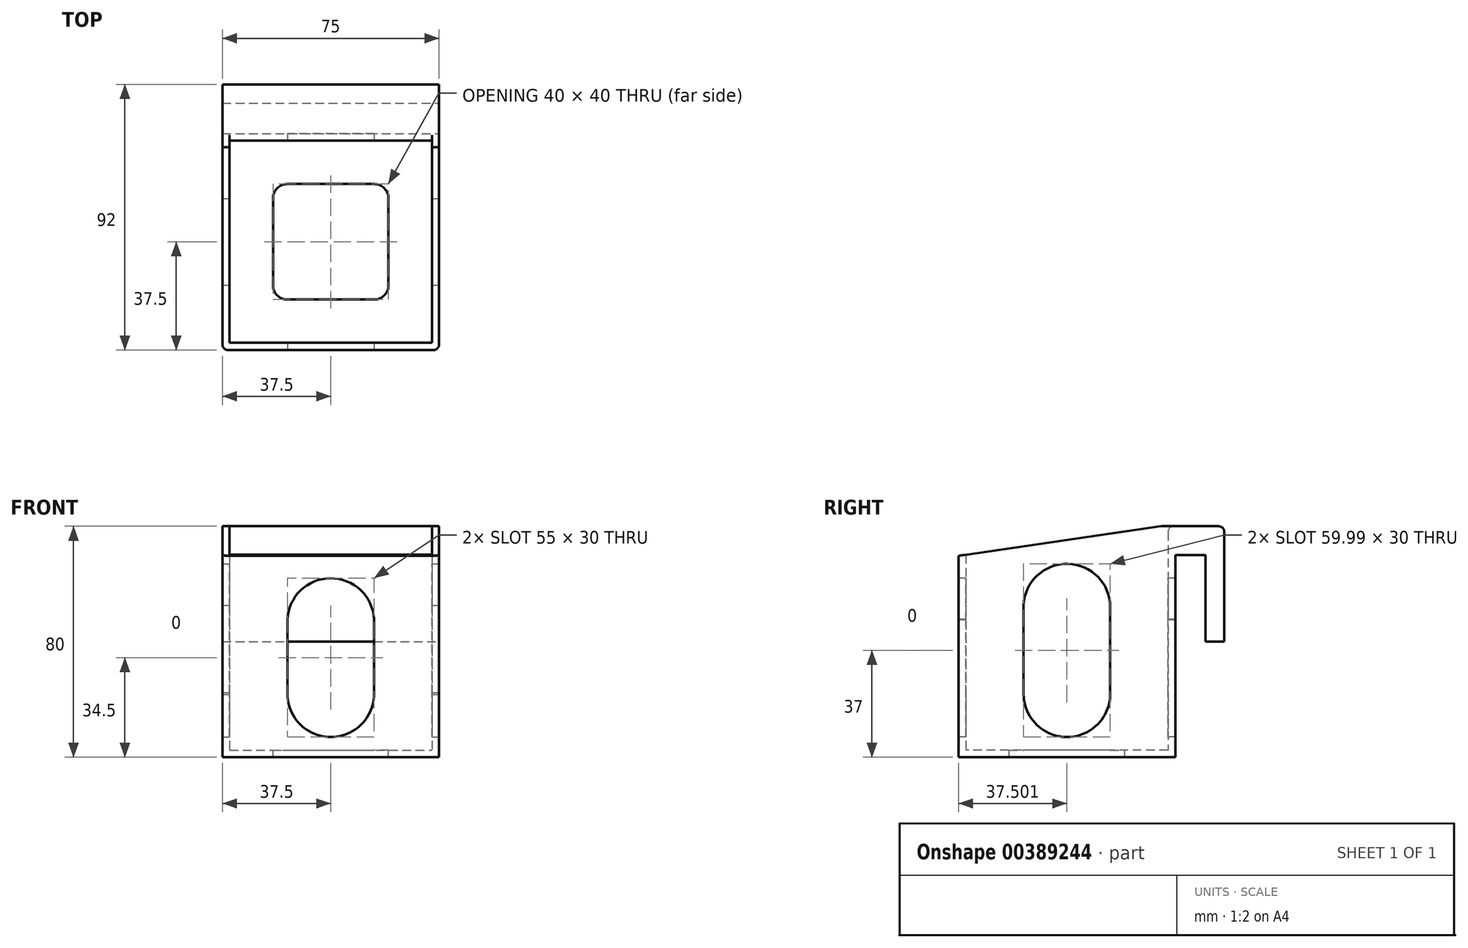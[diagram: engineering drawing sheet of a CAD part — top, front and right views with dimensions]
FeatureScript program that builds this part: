
annotation { "Feature Type Name" : "Feature", "Feature Type Description" : "" }
export const myFeature = defineFeature(function(context is Context, id is Id, definition is map)
    precondition{}
    {
        {
            var Q0;
            Q0=qCreatedBy(makeId("Top.planeOp"),FACE);
            var sketch = newSketch(context, id + "F0", { "sketchPlane" : qUnion([Q0])});
            skLineSegment(sketch, "E0.bottom", {"start": v(-35, 35) * mm, "end": v(35, 35) * mm});
            skLineSegment(sketch, "E0.top", {"start": v(-35, -35) * mm, "end": v(35, -35) * mm});
            skLineSegment(sketch, "E0.left", {"start": v(-35, 35) * mm, "end": v(-35, -35) * mm});
            skLineSegment(sketch, "E0.right", {"start": v(35, 35) * mm, "end": v(35, -35) * mm});
            skPoint(sketch, "E0.middle", {"position": v(0, 0) * mm});
            skLineSegment(sketch, "E1.0", {"start": v(-37.5, 37.5) * mm, "end": v(37.5, 37.5) * mm});
            skLineSegment(sketch, "E1.1", {"start": v(-37.5, 37.5) * mm, "end": v(-37.5, -37.5) * mm});
            skLineSegment(sketch, "E1.2", {"start": v(-37.5, -37.5) * mm, "end": v(37.5, -37.5) * mm});
            skLineSegment(sketch, "E1.3", {"start": v(37.5, 37.5) * mm, "end": v(37.5, -37.5) * mm});
            skSolve(sketch);
        }
        {
            var Q0;
            Q0 = qSketchRegion(id + "F0", true);
            var Q1;
            Q1=makeQuery(id+"F0.imprint","IMPRINT",FACE,{"disambiguationData":[TD([[makeQuery(id+"F0.imprint","IMPRINT",EDGE,{"derivedFrom":sQuery(id+"F0.wireOp",EDGE,"E0.bottom")}),-1.0]])]});
            extrude(context, id + "F1", {"entities" : qUnion([Q0, Q1]), "depth" : 80 * mm, "offsetDistance" : 25 * mm});
        }
        {
            var Q0;
            Q0=makeQuery(id+"F1.opExtrude","CAP_FACE",FACE,{"disambiguationData":[OSD([sQuery(id+"F0.wireOp",EDGE,"E1.0"),sQuery(id+"F0.wireOp",EDGE,"E1.1"),sQuery(id+"F0.wireOp",EDGE,"E1.2"),sQuery(id+"F0.wireOp",EDGE,"E1.3")])],"isStart":false});
            shell(context, id + "F2", {"entities" : qUnion([Q0]), "thickness" : 2.5 * mm});
        }
        {
            var Q0;
            Q0=makeQuery(id+"F1.opExtrude","SWEPT_FACE",FACE,{"disambiguationData":[OSD([sQuery(id+"F0.wireOp",EDGE,"E1.1")])]});
            var sketch = newSketch(context, id + "F3", { "sketchPlane" : qUnion([Q0])});
            skLineSegment(sketch, "E2", {"start": v(-32.69, 80) * mm, "end": v(37.5, 69.78) * mm});
            skLineSegment(sketch, "E3", {"start": v(37.5, 69.78) * mm, "end": v(37.5, 80) * mm});
            skLineSegment(sketch, "E4", {"start": v(37.5, 80) * mm, "end": v(-32.69, 80) * mm});
            skSolve(sketch);
        }
        {
            var Q0;
            Q0 = qSketchRegion(id + "F3", true);
            extrude(context, id + "F4", {"entities" : qUnion([Q0]), "operationType" : NewBodyOperationType.REMOVE, "endBound" : BoundingType.THROUGH_ALL, "oppositeDirection" : true, "depth" : 25 * mm, "offsetDistance" : 25 * mm});
        }
        {
            var Q0;
            Q0=makeQuery(id+"F1.opExtrude","SWEPT_FACE",FACE,{"disambiguationData":[OSD([sQuery(id+"F0.wireOp",EDGE,"E1.0")])]});
            var sketch = newSketch(context, id + "F5", { "sketchPlane" : qUnion([Q0])});
            skLineSegment(sketch, "E5.bottom", {"start": v(-37.5, 80) * mm, "end": v(37.5, 80) * mm});
            skLineSegment(sketch, "E5.top", {"start": v(-37.5, 40) * mm, "end": v(37.5, 40) * mm});
            skLineSegment(sketch, "E5.left", {"start": v(-37.5, 80) * mm, "end": v(-37.5, 40) * mm});
            skLineSegment(sketch, "E5.right", {"start": v(37.5, 80) * mm, "end": v(37.5, 40) * mm});
            skSolve(sketch);
        }
        {
            var Q0;
            Q0 = qSketchRegion(id + "F5", true);
            extrude(context, id + "F6", {"entities" : qUnion([Q0]), "operationType" : NewBodyOperationType.ADD, "depth" : 17 * mm, "offsetDistance" : 25 * mm});
        }
        {
            var Q0;
            Q0=makeQuery(id+"F6.opExtrude","SWEPT_FACE",FACE,{"disambiguationData":[OSD([sQuery(id+"F5.wireOp",EDGE,"E5.top")])]});
            var sketch = newSketch(context, id + "F7", { "sketchPlane" : qUnion([Q0])});
            skLineSegment(sketch, "E6.bottom", {"start": v(-37.5, -37.5) * mm, "end": v(37.5, -37.5) * mm});
            skLineSegment(sketch, "E6.top", {"start": v(-37.5, -48) * mm, "end": v(37.5, -48) * mm});
            skLineSegment(sketch, "E6.left", {"start": v(-37.5, -37.5) * mm, "end": v(-37.5, -48) * mm});
            skLineSegment(sketch, "E6.right", {"start": v(37.5, -37.5) * mm, "end": v(37.5, -48) * mm});
            skSolve(sketch);
        }
        {
            var Q0;
            Q0 = qSketchRegion(id + "F7", true);
            extrude(context, id + "F8", {"entities" : qUnion([Q0]), "operationType" : NewBodyOperationType.REMOVE, "oppositeDirection" : true, "depth" : 30 * mm, "offsetDistance" : 25 * mm});
        }
        {
            var Q0;
            Q0=makeQuery(id+"F6.opExtrude","CAP_EDGE",EDGE,{"disambiguationData":[OSD([sQuery(id+"F5.wireOp",EDGE,"E5.bottom")])],"isStart":false});
            var Q1;
            Q1=makeQuery(id+"F1.opExtrude","SWEPT_EDGE",EDGE,{"disambiguationData":[OSD([sQuery(id+"F0.wireOp",EDGE,"E1.1"),sQuery(id+"F0.wireOp",EDGE,"E1.2")])]});
            var Q2;
            Q2=makeQuery(id+"F1.opExtrude","SWEPT_EDGE",EDGE,{"disambiguationData":[OSD([sQuery(id+"F0.wireOp",EDGE,"E1.2"),sQuery(id+"F0.wireOp",EDGE,"E1.3")])]});
            var Q3;
            {var subQ0=sQuery(id+"F0.wireOp",EDGE,"E1.0");Q3=makeQuery(id+"F2.opShell","OFFSET_EDGE",EDGE,{"disambiguationData":[OSD([subQ0]),TDD([makeQuery(id+"F1.opExtrude","CAP_EDGE",EDGE,{"disambiguationData":[OSD([subQ0])],"isStart":false})])]});}
            fillet(context, id + "F9", {"entities" : qUnion([Q0, Q1, Q2, Q3]), "radius" : 2 * mm, "tangentPropagation" : true, "allowEdgeOverflow" : false});
        }
        {
            var Q0;
            Q0=makeQuery(id+"F6.boolean.opBoolean","MERGE",FACE,{"derivedFrom":[makeQuery(id+"F1.opExtrude","SWEPT_FACE",FACE,{"disambiguationData":[OSD([sQuery(id+"F0.wireOp",EDGE,"E1.3")])]}),makeQuery(id+"F6.opExtrude","SWEPT_FACE",FACE,{"disambiguationData":[OSD([sQuery(id+"F5.wireOp",EDGE,"E5.left")])]})]});
            var sketch = newSketch(context, id + "F10", { "sketchPlane" : qUnion([Q0])});
            skArc(sketch, "E7", {"start": v(-15, 21.8) * mm, "mid": v(0.29, 7) * mm, "end": v(15, 22.38) * mm});
            skArc(sketch, "E8", {"start": v(15, 51.98) * mm, "mid": v(0.3, 67) * mm, "end": v(-14.99, 52.58) * mm});
            skLineSegment(sketch, "E9", {"start": v(-14.99, 52.58) * mm, "end": v(-15, 21.8) * mm});
            skLineSegment(sketch, "E10", {"start": v(15, 22.38) * mm, "end": v(15, 51.98) * mm});
            skSolve(sketch);
        }
        {
            var Q0;
            Q0 = qSketchRegion(id + "F10", true);
            extrude(context, id + "F11", {"entities" : qUnion([Q0]), "operationType" : NewBodyOperationType.REMOVE, "endBound" : BoundingType.THROUGH_ALL, "oppositeDirection" : true, "depth" : 25 * mm, "offsetDistance" : 25 * mm});
        }
        {
            var Q0;
            Q0=makeQuery(id+"F1.opExtrude","SWEPT_FACE",FACE,{"disambiguationData":[OSD([sQuery(id+"F0.wireOp",EDGE,"E1.2")])]});
            var sketch = newSketch(context, id + "F12", { "sketchPlane" : qUnion([Q0])});
            skArc(sketch, "E11", {"start": v(-15, 22) * mm, "mid": v(0, 7) * mm, "end": v(15, 22.01) * mm});
            skArc(sketch, "E12", {"start": v(14.98, 47.75) * mm, "mid": v(-0.09, 62) * mm, "end": v(-14.99, 47.57) * mm});
            skLineSegment(sketch, "E13", {"start": v(-14.99, 47.57) * mm, "end": v(-15, 22) * mm});
            skLineSegment(sketch, "E14", {"start": v(14.98, 47.75) * mm, "end": v(15, 22.01) * mm});
            skSolve(sketch);
        }
        {
            var Q0;
            Q0 = qSketchRegion(id + "F12", true);
            extrude(context, id + "F13", {"entities" : qUnion([Q0]), "operationType" : NewBodyOperationType.REMOVE, "oppositeDirection" : true, "depth" : 80.6 * mm, "offsetDistance" : 25 * mm});
        }
        {
            var Q0;
            Q0=makeQuery(id+"F2.opShell","OFFSET_FACE",FACE,{"disambiguationData":[OSD([sQuery(id+"F0.wireOp",EDGE,"E1.0"),sQuery(id+"F0.wireOp",EDGE,"E1.1"),sQuery(id+"F0.wireOp",EDGE,"E1.2"),sQuery(id+"F0.wireOp",EDGE,"E1.3")])]});
            var sketch = newSketch(context, id + "F14", { "sketchPlane" : qUnion([Q0])});
            skLineSegment(sketch, "E15.bottom", {"start": v(-15, 20) * mm, "end": v(15, 20) * mm});
            skLineSegment(sketch, "E15.top", {"start": v(-15, -20) * mm, "end": v(15, -20) * mm});
            skLineSegment(sketch, "E15.left", {"start": v(-20, 15) * mm, "end": v(-20, -15) * mm});
            skLineSegment(sketch, "E15.right", {"start": v(20, 15) * mm, "end": v(20, -15) * mm});
            skPoint(sketch, "E15.middle", {"position": v(0, 0) * mm});
            skPoint(sketch, "E16.visualSharp", {"position": v(-20, 20) * mm});
            skArc(sketch, "E16.filletArc", {"start": v(-15, 20) * mm, "mid": v(-18.54, 18.54) * mm, "end": v(-20, 15) * mm});
            skPoint(sketch, "E17.visualSharp", {"position": v(20, 20) * mm});
            skArc(sketch, "E17.filletArc", {"start": v(20, 15) * mm, "mid": v(18.54, 18.54) * mm, "end": v(15, 20) * mm});
            skPoint(sketch, "E18.visualSharp", {"position": v(20, -20) * mm});
            skArc(sketch, "E18.filletArc", {"start": v(15, -20) * mm, "mid": v(18.54, -18.54) * mm, "end": v(20, -15) * mm});
            skPoint(sketch, "E19.visualSharp", {"position": v(-20, -20) * mm});
            skArc(sketch, "E19.filletArc", {"start": v(-20, -15) * mm, "mid": v(-18.54, -18.54) * mm, "end": v(-15, -20) * mm});
            skSolve(sketch);
        }
        {
            var Q0;
            Q0 = qSketchRegion(id + "F14", true);
            extrude(context, id + "F15", {"entities" : qUnion([Q0]), "operationType" : NewBodyOperationType.REMOVE, "endBound" : BoundingType.THROUGH_ALL, "oppositeDirection" : true, "depth" : 25 * mm, "offsetDistance" : 25 * mm});
        }
    });
